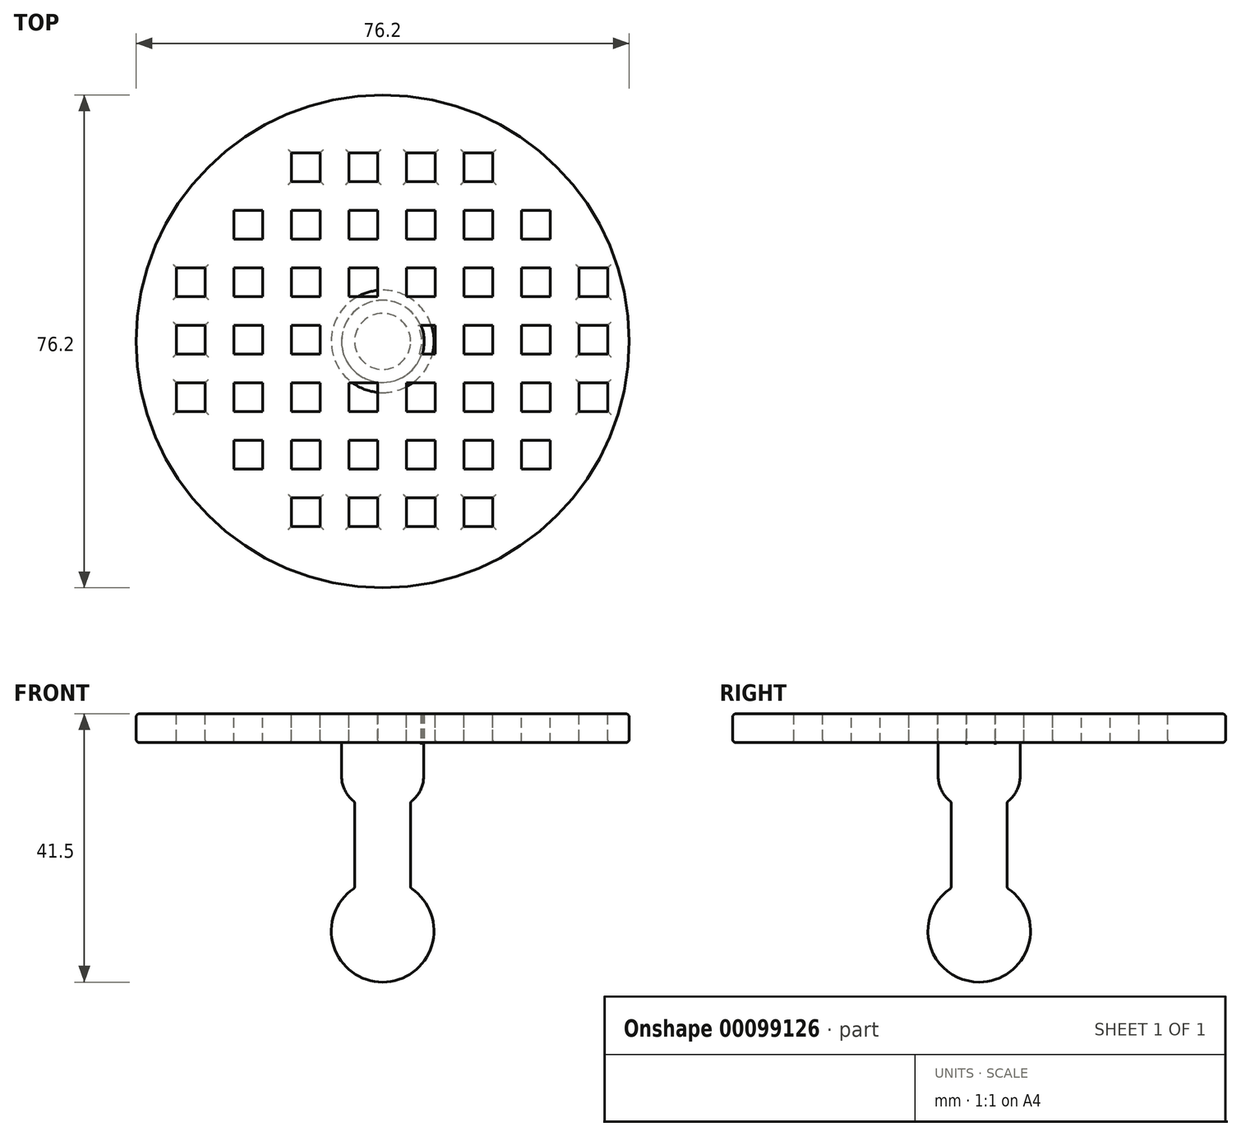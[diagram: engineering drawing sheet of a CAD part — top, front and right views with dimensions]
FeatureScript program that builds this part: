
annotation { "Feature Type Name" : "Feature", "Feature Type Description" : "" }
export const myFeature = defineFeature(function(context is Context, id is Id, definition is map)
    precondition{}
    {
        {
            var Q0;
            Q0=qCreatedBy(makeId("Top.planeOp"),FACE);
            var sketch = newSketch(context, id + "F0", { "sketchPlane" : qUnion([Q0])});
            skCircle(sketch, "E0", {"center": v(0, 0) * mm, "radius": 38.1 * mm});
            skSolve(sketch);
        }
        {
            var Q0;
            Q0=makeQuery(id+"F0.imprint","IMPRINT",FACE,{"disambiguationData":[TD([[makeQuery(id+"F0.imprint","IMPRINT",EDGE,{"derivedFrom":sQuery(id+"F0.wireOp",EDGE,"E0")}),1.0]])]});
            extrude(context, id + "F1", {"entities" : qUnion([Q0]), "depth" : 4.44 * mm});
        }
        {
            var Q0;
            Q0=qCreatedBy(makeId("Top.planeOp"),FACE);
            var sketch = newSketch(context, id + "F2", { "sketchPlane" : qUnion([Q0])});
            skLineSegment(sketch, "E1.bottom", {"start": v(17.03, 29.17) * mm, "end": v(12.58, 29.17) * mm});
            skLineSegment(sketch, "E1.top", {"start": v(17.03, 24.73) * mm, "end": v(12.58, 24.73) * mm});
            skLineSegment(sketch, "E1.left", {"start": v(17.03, 29.17) * mm, "end": v(17.03, 24.73) * mm});
            skLineSegment(sketch, "E1.right", {"start": v(12.58, 29.17) * mm, "end": v(12.58, 24.73) * mm});
            skLineSegment(sketch, "E2.0.1.0", {"start": v(12.58, 20.28) * mm, "end": v(12.58, 15.84) * mm});
            skLineSegment(sketch, "E2.0.1.1", {"start": v(17.03, 20.28) * mm, "end": v(17.03, 15.84) * mm});
            skLineSegment(sketch, "E2.0.1.2", {"start": v(17.03, 20.28) * mm, "end": v(12.58, 20.28) * mm});
            skLineSegment(sketch, "E2.0.1.3", {"start": v(17.03, 15.84) * mm, "end": v(12.58, 15.84) * mm});
            skLineSegment(sketch, "E2.0.2.0", {"start": v(12.58, 11.4) * mm, "end": v(12.58, 6.95) * mm});
            skLineSegment(sketch, "E2.0.2.1", {"start": v(17.03, 11.4) * mm, "end": v(17.03, 6.95) * mm});
            skLineSegment(sketch, "E2.0.2.2", {"start": v(17.03, 11.4) * mm, "end": v(12.58, 11.4) * mm});
            skLineSegment(sketch, "E2.0.2.3", {"start": v(17.03, 6.95) * mm, "end": v(12.58, 6.95) * mm});
            skLineSegment(sketch, "E2.0.3.0", {"start": v(12.58, 2.5) * mm, "end": v(12.58, -1.94) * mm});
            skLineSegment(sketch, "E2.0.3.1", {"start": v(17.03, 2.5) * mm, "end": v(17.03, -1.94) * mm});
            skLineSegment(sketch, "E2.0.3.2", {"start": v(17.03, 2.5) * mm, "end": v(12.58, 2.5) * mm});
            skLineSegment(sketch, "E2.0.3.3", {"start": v(17.03, -1.94) * mm, "end": v(12.58, -1.94) * mm});
            skLineSegment(sketch, "E2.0.4.0", {"start": v(12.58, -6.39) * mm, "end": v(12.58, -10.83) * mm});
            skLineSegment(sketch, "E2.0.4.1", {"start": v(17.03, -6.39) * mm, "end": v(17.03, -10.83) * mm});
            skLineSegment(sketch, "E2.0.4.2", {"start": v(17.03, -6.39) * mm, "end": v(12.58, -6.39) * mm});
            skLineSegment(sketch, "E2.0.4.3", {"start": v(17.03, -10.83) * mm, "end": v(12.58, -10.83) * mm});
            skLineSegment(sketch, "E2.0.5.0", {"start": v(12.58, -15.28) * mm, "end": v(12.58, -19.72) * mm});
            skLineSegment(sketch, "E2.0.5.1", {"start": v(17.03, -15.28) * mm, "end": v(17.03, -19.72) * mm});
            skLineSegment(sketch, "E2.0.5.2", {"start": v(17.03, -15.28) * mm, "end": v(12.58, -15.28) * mm});
            skLineSegment(sketch, "E2.0.5.3", {"start": v(17.03, -19.72) * mm, "end": v(12.58, -19.72) * mm});
            skLineSegment(sketch, "E2.0.6.0", {"start": v(12.58, -24.17) * mm, "end": v(12.58, -28.61) * mm});
            skLineSegment(sketch, "E2.0.6.1", {"start": v(17.03, -24.17) * mm, "end": v(17.03, -28.61) * mm});
            skLineSegment(sketch, "E2.0.6.2", {"start": v(17.03, -24.17) * mm, "end": v(12.58, -24.17) * mm});
            skLineSegment(sketch, "E2.0.6.3", {"start": v(17.03, -28.61) * mm, "end": v(12.58, -28.61) * mm});
            skLineSegment(sketch, "E2.1.0.0", {"start": v(3.7, 29.17) * mm, "end": v(3.7, 24.73) * mm});
            skLineSegment(sketch, "E2.1.0.1", {"start": v(8.14, 29.17) * mm, "end": v(8.14, 24.73) * mm});
            skLineSegment(sketch, "E2.1.0.2", {"start": v(8.14, 29.17) * mm, "end": v(3.7, 29.17) * mm});
            skLineSegment(sketch, "E2.1.0.3", {"start": v(8.14, 24.73) * mm, "end": v(3.7, 24.73) * mm});
            skLineSegment(sketch, "E2.1.1.0", {"start": v(3.7, 20.28) * mm, "end": v(3.7, 15.84) * mm});
            skLineSegment(sketch, "E2.1.1.1", {"start": v(8.14, 20.28) * mm, "end": v(8.14, 15.84) * mm});
            skLineSegment(sketch, "E2.1.1.2", {"start": v(8.14, 20.28) * mm, "end": v(3.7, 20.28) * mm});
            skLineSegment(sketch, "E2.1.1.3", {"start": v(8.14, 15.84) * mm, "end": v(3.7, 15.84) * mm});
            skLineSegment(sketch, "E2.1.2.0", {"start": v(3.7, 11.4) * mm, "end": v(3.7, 6.95) * mm});
            skLineSegment(sketch, "E2.1.2.1", {"start": v(8.14, 11.4) * mm, "end": v(8.14, 6.95) * mm});
            skLineSegment(sketch, "E2.1.2.2", {"start": v(8.14, 11.4) * mm, "end": v(3.7, 11.4) * mm});
            skLineSegment(sketch, "E2.1.2.3", {"start": v(8.14, 6.95) * mm, "end": v(3.7, 6.95) * mm});
            skLineSegment(sketch, "E2.1.3.0", {"start": v(3.7, 2.5) * mm, "end": v(3.7, -1.94) * mm});
            skLineSegment(sketch, "E2.1.3.1", {"start": v(8.14, 2.5) * mm, "end": v(8.14, -1.94) * mm});
            skLineSegment(sketch, "E2.1.3.2", {"start": v(8.14, 2.5) * mm, "end": v(3.7, 2.5) * mm});
            skLineSegment(sketch, "E2.1.3.3", {"start": v(8.14, -1.94) * mm, "end": v(3.7, -1.94) * mm});
            skLineSegment(sketch, "E2.1.4.0", {"start": v(3.7, -6.39) * mm, "end": v(3.7, -10.83) * mm});
            skLineSegment(sketch, "E2.1.4.1", {"start": v(8.14, -6.39) * mm, "end": v(8.14, -10.83) * mm});
            skLineSegment(sketch, "E2.1.4.2", {"start": v(8.14, -6.39) * mm, "end": v(3.7, -6.39) * mm});
            skLineSegment(sketch, "E2.1.4.3", {"start": v(8.14, -10.83) * mm, "end": v(3.7, -10.83) * mm});
            skLineSegment(sketch, "E2.1.5.0", {"start": v(3.7, -15.28) * mm, "end": v(3.7, -19.72) * mm});
            skLineSegment(sketch, "E2.1.5.1", {"start": v(8.14, -15.28) * mm, "end": v(8.14, -19.72) * mm});
            skLineSegment(sketch, "E2.1.5.2", {"start": v(8.14, -15.28) * mm, "end": v(3.7, -15.28) * mm});
            skLineSegment(sketch, "E2.1.5.3", {"start": v(8.14, -19.72) * mm, "end": v(3.7, -19.72) * mm});
            skLineSegment(sketch, "E2.1.6.0", {"start": v(3.7, -24.17) * mm, "end": v(3.7, -28.61) * mm});
            skLineSegment(sketch, "E2.1.6.1", {"start": v(8.14, -24.17) * mm, "end": v(8.14, -28.61) * mm});
            skLineSegment(sketch, "E2.1.6.2", {"start": v(8.14, -24.17) * mm, "end": v(3.7, -24.17) * mm});
            skLineSegment(sketch, "E2.1.6.3", {"start": v(8.14, -28.61) * mm, "end": v(3.7, -28.61) * mm});
            skLineSegment(sketch, "E2.2.0.0", {"start": v(-5.2, 29.17) * mm, "end": v(-5.2, 24.73) * mm});
            skLineSegment(sketch, "E2.2.0.1", {"start": v(-0.75, 29.17) * mm, "end": v(-0.75, 24.73) * mm});
            skLineSegment(sketch, "E2.2.0.2", {"start": v(-0.75, 29.17) * mm, "end": v(-5.2, 29.17) * mm});
            skLineSegment(sketch, "E2.2.0.3", {"start": v(-0.75, 24.73) * mm, "end": v(-5.2, 24.73) * mm});
            skLineSegment(sketch, "E2.2.1.0", {"start": v(-5.2, 20.28) * mm, "end": v(-5.2, 15.84) * mm});
            skLineSegment(sketch, "E2.2.1.1", {"start": v(-0.75, 20.28) * mm, "end": v(-0.75, 15.84) * mm});
            skLineSegment(sketch, "E2.2.1.2", {"start": v(-0.75, 20.28) * mm, "end": v(-5.2, 20.28) * mm});
            skLineSegment(sketch, "E2.2.1.3", {"start": v(-0.75, 15.84) * mm, "end": v(-5.2, 15.84) * mm});
            skLineSegment(sketch, "E2.2.2.0", {"start": v(-5.2, 11.4) * mm, "end": v(-5.2, 6.95) * mm});
            skLineSegment(sketch, "E2.2.2.1", {"start": v(-0.75, 11.4) * mm, "end": v(-0.75, 6.95) * mm});
            skLineSegment(sketch, "E2.2.2.2", {"start": v(-0.75, 11.4) * mm, "end": v(-5.2, 11.4) * mm});
            skLineSegment(sketch, "E2.2.2.3", {"start": v(-0.75, 6.95) * mm, "end": v(-5.2, 6.95) * mm});
            skLineSegment(sketch, "E2.2.3.0", {"start": v(-5.2, 2.5) * mm, "end": v(-5.2, -1.94) * mm});
            skLineSegment(sketch, "E2.2.3.1", {"start": v(-0.75, 2.5) * mm, "end": v(-0.75, -1.94) * mm});
            skLineSegment(sketch, "E2.2.3.2", {"start": v(-0.75, 2.5) * mm, "end": v(-5.2, 2.5) * mm});
            skLineSegment(sketch, "E2.2.3.3", {"start": v(-0.75, -1.94) * mm, "end": v(-5.2, -1.94) * mm});
            skLineSegment(sketch, "E2.2.4.0", {"start": v(-5.2, -6.39) * mm, "end": v(-5.2, -10.83) * mm});
            skLineSegment(sketch, "E2.2.4.1", {"start": v(-0.75, -6.39) * mm, "end": v(-0.75, -10.83) * mm});
            skLineSegment(sketch, "E2.2.4.2", {"start": v(-0.75, -6.39) * mm, "end": v(-5.2, -6.39) * mm});
            skLineSegment(sketch, "E2.2.4.3", {"start": v(-0.75, -10.83) * mm, "end": v(-5.2, -10.83) * mm});
            skLineSegment(sketch, "E2.2.5.0", {"start": v(-5.2, -15.28) * mm, "end": v(-5.2, -19.72) * mm});
            skLineSegment(sketch, "E2.2.5.1", {"start": v(-0.75, -15.28) * mm, "end": v(-0.75, -19.72) * mm});
            skLineSegment(sketch, "E2.2.5.2", {"start": v(-0.75, -15.28) * mm, "end": v(-5.2, -15.28) * mm});
            skLineSegment(sketch, "E2.2.5.3", {"start": v(-0.75, -19.72) * mm, "end": v(-5.2, -19.72) * mm});
            skLineSegment(sketch, "E2.2.6.0", {"start": v(-5.2, -24.17) * mm, "end": v(-5.2, -28.61) * mm});
            skLineSegment(sketch, "E2.2.6.1", {"start": v(-0.75, -24.17) * mm, "end": v(-0.75, -28.61) * mm});
            skLineSegment(sketch, "E2.2.6.2", {"start": v(-0.75, -24.17) * mm, "end": v(-5.2, -24.17) * mm});
            skLineSegment(sketch, "E2.2.6.3", {"start": v(-0.75, -28.61) * mm, "end": v(-5.2, -28.61) * mm});
            skLineSegment(sketch, "E2.3.0.0", {"start": v(-14.09, 29.17) * mm, "end": v(-14.09, 24.73) * mm});
            skLineSegment(sketch, "E2.3.0.1", {"start": v(-9.64, 29.17) * mm, "end": v(-9.64, 24.73) * mm});
            skLineSegment(sketch, "E2.3.0.2", {"start": v(-9.64, 29.17) * mm, "end": v(-14.09, 29.17) * mm});
            skLineSegment(sketch, "E2.3.0.3", {"start": v(-9.64, 24.73) * mm, "end": v(-14.09, 24.73) * mm});
            skLineSegment(sketch, "E2.3.1.0", {"start": v(-14.09, 20.28) * mm, "end": v(-14.09, 15.84) * mm});
            skLineSegment(sketch, "E2.3.1.1", {"start": v(-9.64, 20.28) * mm, "end": v(-9.64, 15.84) * mm});
            skLineSegment(sketch, "E2.3.1.2", {"start": v(-9.64, 20.28) * mm, "end": v(-14.09, 20.28) * mm});
            skLineSegment(sketch, "E2.3.1.3", {"start": v(-9.64, 15.84) * mm, "end": v(-14.09, 15.84) * mm});
            skLineSegment(sketch, "E2.3.2.0", {"start": v(-14.09, 11.4) * mm, "end": v(-14.09, 6.95) * mm});
            skLineSegment(sketch, "E2.3.2.1", {"start": v(-9.64, 11.4) * mm, "end": v(-9.64, 6.95) * mm});
            skLineSegment(sketch, "E2.3.2.2", {"start": v(-9.64, 11.4) * mm, "end": v(-14.09, 11.4) * mm});
            skLineSegment(sketch, "E2.3.2.3", {"start": v(-9.64, 6.95) * mm, "end": v(-14.09, 6.95) * mm});
            skLineSegment(sketch, "E2.3.3.0", {"start": v(-14.09, 2.5) * mm, "end": v(-14.09, -1.94) * mm});
            skLineSegment(sketch, "E2.3.3.1", {"start": v(-9.64, 2.5) * mm, "end": v(-9.64, -1.94) * mm});
            skLineSegment(sketch, "E2.3.3.2", {"start": v(-9.64, 2.5) * mm, "end": v(-14.09, 2.5) * mm});
            skLineSegment(sketch, "E2.3.3.3", {"start": v(-9.64, -1.94) * mm, "end": v(-14.09, -1.94) * mm});
            skLineSegment(sketch, "E2.3.4.0", {"start": v(-14.09, -6.39) * mm, "end": v(-14.09, -10.83) * mm});
            skLineSegment(sketch, "E2.3.4.1", {"start": v(-9.64, -6.39) * mm, "end": v(-9.64, -10.83) * mm});
            skLineSegment(sketch, "E2.3.4.2", {"start": v(-9.64, -6.39) * mm, "end": v(-14.09, -6.39) * mm});
            skLineSegment(sketch, "E2.3.4.3", {"start": v(-9.64, -10.83) * mm, "end": v(-14.09, -10.83) * mm});
            skLineSegment(sketch, "E2.3.5.0", {"start": v(-14.09, -15.28) * mm, "end": v(-14.09, -19.72) * mm});
            skLineSegment(sketch, "E2.3.5.1", {"start": v(-9.64, -15.28) * mm, "end": v(-9.64, -19.72) * mm});
            skLineSegment(sketch, "E2.3.5.2", {"start": v(-9.64, -15.28) * mm, "end": v(-14.09, -15.28) * mm});
            skLineSegment(sketch, "E2.3.5.3", {"start": v(-9.64, -19.72) * mm, "end": v(-14.09, -19.72) * mm});
            skLineSegment(sketch, "E2.3.6.0", {"start": v(-14.09, -24.17) * mm, "end": v(-14.09, -28.61) * mm});
            skLineSegment(sketch, "E2.3.6.1", {"start": v(-9.64, -24.17) * mm, "end": v(-9.64, -28.61) * mm});
            skLineSegment(sketch, "E2.3.6.2", {"start": v(-9.64, -24.17) * mm, "end": v(-14.09, -24.17) * mm});
            skLineSegment(sketch, "E2.3.6.3", {"start": v(-9.64, -28.61) * mm, "end": v(-14.09, -28.61) * mm});
            skLineSegment(sketch, "E2.direction1", {"start": v(12.58, 24.73) * mm, "end": v(3.7, 24.73) * mm, "construction": true});
            skLineSegment(sketch, "E2.direction2", {"start": v(12.58, 24.73) * mm, "end": v(12.58, 15.84) * mm, "construction": true});
            skLineSegment(sketch, "E3.1.0.0", {"start": v(-18.53, 20.28) * mm, "end": v(-22.98, 20.28) * mm});
            skLineSegment(sketch, "E3.1.0.1", {"start": v(-18.53, 15.84) * mm, "end": v(-22.98, 15.84) * mm});
            skLineSegment(sketch, "E3.1.0.2", {"start": v(-18.53, 20.28) * mm, "end": v(-18.53, 15.84) * mm});
            skLineSegment(sketch, "E3.1.0.3", {"start": v(-18.53, 11.4) * mm, "end": v(-22.98, 11.4) * mm});
            skLineSegment(sketch, "E3.1.0.4", {"start": v(-18.53, 11.4) * mm, "end": v(-18.53, 6.95) * mm});
            skLineSegment(sketch, "E3.1.0.5", {"start": v(-22.98, 11.4) * mm, "end": v(-22.98, 6.95) * mm});
            skLineSegment(sketch, "E3.1.0.6", {"start": v(-18.53, 6.95) * mm, "end": v(-22.98, 6.95) * mm});
            skLineSegment(sketch, "E3.1.0.7", {"start": v(-18.53, 2.5) * mm, "end": v(-22.98, 2.5) * mm});
            skLineSegment(sketch, "E3.1.0.8", {"start": v(-18.53, -1.94) * mm, "end": v(-22.98, -1.94) * mm});
            skLineSegment(sketch, "E3.1.0.9", {"start": v(-18.53, 2.5) * mm, "end": v(-18.53, -1.94) * mm});
            skLineSegment(sketch, "E3.1.0.10", {"start": v(-22.98, 2.5) * mm, "end": v(-22.98, -1.94) * mm});
            skLineSegment(sketch, "E3.1.0.11", {"start": v(-18.53, -6.39) * mm, "end": v(-22.98, -6.39) * mm});
            skLineSegment(sketch, "E3.1.0.12", {"start": v(-18.53, -6.39) * mm, "end": v(-18.53, -10.83) * mm});
            skLineSegment(sketch, "E3.1.0.13", {"start": v(-22.98, -6.39) * mm, "end": v(-22.98, -10.83) * mm});
            skLineSegment(sketch, "E3.1.0.14", {"start": v(-18.53, -10.83) * mm, "end": v(-22.98, -10.83) * mm});
            skLineSegment(sketch, "E3.1.0.15", {"start": v(-18.53, -15.28) * mm, "end": v(-22.98, -15.28) * mm});
            skLineSegment(sketch, "E3.1.0.16", {"start": v(-18.53, -15.28) * mm, "end": v(-18.53, -19.72) * mm});
            skLineSegment(sketch, "E3.1.0.17", {"start": v(-22.98, -15.28) * mm, "end": v(-22.98, -19.72) * mm});
            skLineSegment(sketch, "E3.1.0.18", {"start": v(-18.53, -19.72) * mm, "end": v(-22.98, -19.72) * mm});
            skLineSegment(sketch, "E3.direction1", {"start": v(-14.09, 20.28) * mm, "end": v(-22.98, 20.28) * mm, "construction": true});
            skLineSegment(sketch, "E4.1.0.0", {"start": v(25.92, 15.84) * mm, "end": v(21.47, 15.84) * mm});
            skLineSegment(sketch, "E4.1.0.1", {"start": v(25.92, 20.28) * mm, "end": v(21.47, 20.28) * mm});
            skLineSegment(sketch, "E4.1.0.2", {"start": v(25.92, 20.28) * mm, "end": v(25.92, 15.84) * mm});
            skLineSegment(sketch, "E4.1.0.3", {"start": v(21.47, 20.28) * mm, "end": v(21.47, 15.84) * mm});
            skLineSegment(sketch, "E4.1.0.4", {"start": v(21.47, 11.4) * mm, "end": v(21.47, 6.95) * mm});
            skLineSegment(sketch, "E4.1.0.5", {"start": v(25.92, 6.95) * mm, "end": v(21.47, 6.95) * mm});
            skLineSegment(sketch, "E4.1.0.6", {"start": v(25.92, 11.4) * mm, "end": v(21.47, 11.4) * mm});
            skLineSegment(sketch, "E4.1.0.7", {"start": v(25.92, 11.4) * mm, "end": v(25.92, 6.95) * mm});
            skLineSegment(sketch, "E4.1.0.8", {"start": v(25.92, 2.5) * mm, "end": v(21.47, 2.5) * mm});
            skLineSegment(sketch, "E4.1.0.9", {"start": v(21.47, 2.5) * mm, "end": v(21.47, -1.94) * mm});
            skLineSegment(sketch, "E4.1.0.10", {"start": v(25.92, -1.94) * mm, "end": v(21.47, -1.94) * mm});
            skLineSegment(sketch, "E4.1.0.11", {"start": v(25.92, 2.5) * mm, "end": v(25.92, -1.94) * mm});
            skLineSegment(sketch, "E4.1.0.12", {"start": v(25.92, -6.39) * mm, "end": v(21.47, -6.39) * mm});
            skLineSegment(sketch, "E4.1.0.13", {"start": v(25.92, -6.39) * mm, "end": v(25.92, -10.83) * mm});
            skLineSegment(sketch, "E4.1.0.14", {"start": v(21.47, -6.39) * mm, "end": v(21.47, -10.83) * mm});
            skLineSegment(sketch, "E4.1.0.15", {"start": v(25.92, -10.83) * mm, "end": v(21.47, -10.83) * mm});
            skLineSegment(sketch, "E4.1.0.16", {"start": v(25.92, -15.28) * mm, "end": v(21.47, -15.28) * mm});
            skLineSegment(sketch, "E4.1.0.17", {"start": v(21.47, -15.28) * mm, "end": v(21.47, -19.72) * mm});
            skLineSegment(sketch, "E4.1.0.18", {"start": v(25.92, -19.72) * mm, "end": v(21.47, -19.72) * mm});
            skLineSegment(sketch, "E4.1.0.19", {"start": v(25.92, -15.28) * mm, "end": v(25.92, -19.72) * mm});
            skLineSegment(sketch, "E4.direction1", {"start": v(12.58, 15.84) * mm, "end": v(21.47, 15.84) * mm, "construction": true});
            skLineSegment(sketch, "E5.1.0.0", {"start": v(-31.87, 11.4) * mm, "end": v(-31.87, 6.95) * mm});
            skLineSegment(sketch, "E5.1.0.1", {"start": v(-27.42, 11.4) * mm, "end": v(-31.87, 11.4) * mm});
            skLineSegment(sketch, "E5.1.0.2", {"start": v(-27.42, 11.4) * mm, "end": v(-27.42, 6.95) * mm});
            skLineSegment(sketch, "E5.1.0.3", {"start": v(-27.42, 6.95) * mm, "end": v(-31.87, 6.95) * mm});
            skLineSegment(sketch, "E5.1.0.4", {"start": v(-27.42, 2.5) * mm, "end": v(-31.87, 2.5) * mm});
            skLineSegment(sketch, "E5.1.0.5", {"start": v(-31.87, 2.5) * mm, "end": v(-31.87, -1.94) * mm});
            skLineSegment(sketch, "E5.1.0.6", {"start": v(-27.42, -1.94) * mm, "end": v(-31.87, -1.94) * mm});
            skLineSegment(sketch, "E5.1.0.7", {"start": v(-27.42, 2.5) * mm, "end": v(-27.42, -1.94) * mm});
            skLineSegment(sketch, "E5.1.0.8", {"start": v(-27.42, -6.39) * mm, "end": v(-31.87, -6.39) * mm});
            skLineSegment(sketch, "E5.1.0.9", {"start": v(-27.42, -10.83) * mm, "end": v(-31.87, -10.83) * mm});
            skLineSegment(sketch, "E5.1.0.10", {"start": v(-31.87, -6.39) * mm, "end": v(-31.87, -10.83) * mm});
            skLineSegment(sketch, "E5.1.0.11", {"start": v(-27.42, -6.39) * mm, "end": v(-27.42, -10.83) * mm});
            skLineSegment(sketch, "E5.direction1", {"start": v(-22.98, 6.95) * mm, "end": v(-31.87, 6.95) * mm, "construction": true});
            skLineSegment(sketch, "E6.1.0.0", {"start": v(34.8, 11.4) * mm, "end": v(30.36, 11.4) * mm});
            skLineSegment(sketch, "E6.1.0.1", {"start": v(34.8, 6.95) * mm, "end": v(30.36, 6.95) * mm});
            skLineSegment(sketch, "E6.1.0.2", {"start": v(30.36, 11.4) * mm, "end": v(30.36, 6.95) * mm});
            skLineSegment(sketch, "E6.1.0.3", {"start": v(34.8, 11.4) * mm, "end": v(34.8, 6.95) * mm});
            skLineSegment(sketch, "E6.1.0.4", {"start": v(34.8, 2.5) * mm, "end": v(30.36, 2.5) * mm});
            skLineSegment(sketch, "E6.1.0.5", {"start": v(34.8, 2.5) * mm, "end": v(34.8, -1.94) * mm});
            skLineSegment(sketch, "E6.1.0.6", {"start": v(30.36, 2.5) * mm, "end": v(30.36, -1.94) * mm});
            skLineSegment(sketch, "E6.1.0.7", {"start": v(34.8, -1.94) * mm, "end": v(30.36, -1.94) * mm});
            skLineSegment(sketch, "E6.1.0.8", {"start": v(34.8, -6.39) * mm, "end": v(30.36, -6.39) * mm});
            skLineSegment(sketch, "E6.1.0.9", {"start": v(30.36, -6.39) * mm, "end": v(30.36, -10.83) * mm});
            skLineSegment(sketch, "E6.1.0.10", {"start": v(34.8, -6.39) * mm, "end": v(34.8, -10.83) * mm});
            skLineSegment(sketch, "E6.direction1", {"start": v(21.47, 11.4) * mm, "end": v(30.36, 11.4) * mm, "construction": true});
            skLineSegment(sketch, "E7", {"start": v(34.8, -10.83) * mm, "end": v(30.36, -10.83) * mm});
            skLineSegment(sketch, "E8", {"start": v(-22.98, 20.28) * mm, "end": v(-22.98, 15.84) * mm});
            skSolve(sketch);
        }
        {
            var Q0;
            Q0 = qSketchRegion(id + "F2", true);
            extrude(context, id + "F3", {"entities" : qUnion([Q0]), "operationType" : NewBodyOperationType.REMOVE, "endBound" : BoundingType.SYMMETRIC, "oppositeDirection" : true, "depth" : 25.4 * mm});
        }
        {
            var Q0;
            Q0=qCreatedBy(makeId("Right.planeOp"),FACE);
            var sketch = newSketch(context, id + "F4", { "sketchPlane" : qUnion([Q0])});
            skLineSegment(sketch, "E9", {"start": v(0, 0) * mm, "end": v(-6.35, 0) * mm});
            skLineSegment(sketch, "E10", {"start": v(-6.35, 0) * mm, "end": v(-6.35, -9.2) * mm});
            skLineSegment(sketch, "E11", {"start": v(-6.35, -9.2) * mm, "end": v(-4.34, -9.2) * mm});
            skLineSegment(sketch, "E12", {"start": v(-4.34, -9.2) * mm, "end": v(-4.34, -22.53) * mm});
            skArc(sketch, "E13", {"start": v(-7.93, -29.12) * mm, "mid": v(-6.97, -25.34) * mm, "end": v(-4.34, -22.48) * mm});
            skPoint(sketch, "E13.startSnap0", {"position": v(-2.3, -29.12) * mm});
            skArc(sketch, "E14", {"start": v(-7.93, -29.12) * mm, "mid": v(-5.6, -34.72) * mm, "end": v(0, -37.05) * mm});
            skLineSegment(sketch, "E15", {"start": v(0, -37.05) * mm, "end": v(0, 0) * mm});
            skSolve(sketch);
        }
        {
            var Q0;
            Q0 = qSketchRegion(id + "F4", true);
            var Q1;
            Q1=sQuery(id+"F4.wireOp",EDGE,"E15");
            revolve(context, id + "F5", {"operationType" : NewBodyOperationType.ADD, "entities" : qUnion([Q0]), "axis" : qUnion([Q1]), "revolveType" : RevolveType.FULL});
        }
        {
            var Q0;
            Q0=makeQuery(id+"F5.opRevolve","SWEPT_EDGE",EDGE,{"disambiguationData":[OSD([sQuery(id+"F4.wireOp",EDGE,"E10"),sQuery(id+"F4.wireOp",EDGE,"E11")])]});
            fillet(context, id + "F6", {"entities" : qUnion([Q0]), "radius" : 5.08 * mm, "tangentPropagation" : true, "allowEdgeOverflow" : false});
        }
        {
            var Q0;
            Q0=makeQuery(id+"F6.opFillet","BLEND_EDGE",EDGE,{"blendedFrom":[makeQuery(id+"F5.opRevolve","SWEPT_EDGE",EDGE,{"disambiguationData":[OSD([sQuery(id+"F4.wireOp",EDGE,"E10"),sQuery(id+"F4.wireOp",EDGE,"E11")])]}),makeQuery(id+"F5.opRevolve","SWEPT_FACE",FACE,{"disambiguationData":[OSD([sQuery(id+"F4.wireOp",EDGE,"E12")])]})],"blendedInto":[makeQuery(id+"F5.opRevolve","SWEPT_FACE",FACE,{"disambiguationData":[OSD([sQuery(id+"F4.wireOp",EDGE,"E12")])]})]});
            var Q1;
            Q1=makeQuery(id+"F5.opRevolve","SWEPT_EDGE",EDGE,{"disambiguationData":[OSD([sQuery(id+"F4.wireOp",EDGE,"E12"),sQuery(id+"F4.wireOp",EDGE,"E13")])]});
            var Q2;
            {var subQ0=sQuery(id+"F4.wireOp",EDGE,"E10");Q2=makeQuery(id+"F5.boolean.opBoolean","SPLIT",EDGE,{"disambiguationData":[topologyDisambiguationEdgeConnected([makeQuery(id+"F1.opExtrude","CAP_FACE",FACE,{"disambiguationData":[OSD([sQuery(id+"F0.wireOp",EDGE,"E0")])],"isStart":true})])],"derivedFrom":makeQuery(id+"F5.opRevolve","SWEPT_EDGE",EDGE,{"disambiguationData":[OSD([sQuery(id+"F4.wireOp",EDGE,"E9"),subQ0])]})});}
            fillet(context, id + "F7", {"entities" : qUnion([Q0, Q1, Q2]), "radius" : 0.32 * mm, "tangentPropagation" : true, "allowEdgeOverflow" : false});
        }
        {
            var Q0;
            Q0=makeQuery(id+"F5.boolean.opBoolean","SPLIT",FACE,{"disambiguationData":[TD([makeQuery(id+"F1.opExtrude","CAP_FACE",FACE,{"disambiguationData":[OSD([sQuery(id+"F0.wireOp",EDGE,"E0")])],"isStart":true})])],"derivedFrom":makeQuery(id+"F5.opRevolve","SWEPT_FACE",FACE,{"disambiguationData":[OSD([sQuery(id+"F4.wireOp",EDGE,"E9")])]})});
            var sketch = newSketch(context, id + "F8", { "sketchPlane" : qUnion([Q0])});
            skCircle(sketch, "E16", {"center": v(0, 0) * mm, "radius": 6.43 * mm});
            skSolve(sketch);
        }
        {
            var Q0;
            Q0 = qSketchRegion(id + "F8", true);
            extrude(context, id + "F9", {"entities" : qUnion([Q0]), "operationType" : NewBodyOperationType.ADD, "depth" : 4.44 * mm});
        }
        {
            var Q0;
            Q0=makeQuery(id+"F1.opExtrude","CAP_EDGE",EDGE,{"disambiguationData":[OSD([sQuery(id+"F0.wireOp",EDGE,"E0")])],"isStart":true});
            var Q1;
            Q1=makeQuery(id+"F1.opExtrude","CAP_EDGE",EDGE,{"disambiguationData":[OSD([sQuery(id+"F0.wireOp",EDGE,"E0")])],"isStart":false});
            fillet(context, id + "F10", {"entities" : qUnion([Q0, Q1]), "radius" : 0.5 * mm, "tangentPropagation" : true, "allowEdgeOverflow" : false});
        }
        {
            var Q0;
            Q0=makeQuery(id+"F3.boolean.opBoolean","INTERSECT",EDGE,{"derivedFrom":[makeQuery(id+"F1.opExtrude","CAP_FACE",FACE,{"disambiguationData":[OSD([sQuery(id+"F0.wireOp",EDGE,"E0")])],"isStart":true}),makeQuery(id+"F3.opExtrude","SWEPT_FACE",FACE,{"disambiguationData":[OSD([sQuery(id+"F2.wireOp",EDGE,"E2.3.6.2")])]})]});
            var Q1;
            Q1=makeQuery(id+"F3.boolean.opBoolean","INTERSECT",EDGE,{"derivedFrom":[makeQuery(id+"F1.opExtrude","CAP_FACE",FACE,{"disambiguationData":[OSD([sQuery(id+"F0.wireOp",EDGE,"E0")])],"isStart":true}),makeQuery(id+"F3.opExtrude","SWEPT_FACE",FACE,{"disambiguationData":[OSD([sQuery(id+"F2.wireOp",EDGE,"E2.3.6.1")])]})]});
            var Q2;
            Q2=makeQuery(id+"F3.boolean.opBoolean","INTERSECT",EDGE,{"derivedFrom":[makeQuery(id+"F1.opExtrude","CAP_FACE",FACE,{"disambiguationData":[OSD([sQuery(id+"F0.wireOp",EDGE,"E0")])],"isStart":true}),makeQuery(id+"F3.opExtrude","SWEPT_FACE",FACE,{"disambiguationData":[OSD([sQuery(id+"F2.wireOp",EDGE,"E2.3.6.3")])]})]});
            var Q3;
            Q3=makeQuery(id+"F3.boolean.opBoolean","INTERSECT",EDGE,{"derivedFrom":[makeQuery(id+"F1.opExtrude","CAP_FACE",FACE,{"disambiguationData":[OSD([sQuery(id+"F0.wireOp",EDGE,"E0")])],"isStart":true}),makeQuery(id+"F3.opExtrude","SWEPT_FACE",FACE,{"disambiguationData":[OSD([sQuery(id+"F2.wireOp",EDGE,"E2.3.6.0")])]})]});
            var Q4;
            Q4=makeQuery(id+"F3.boolean.opBoolean","INTERSECT",EDGE,{"derivedFrom":[makeQuery(id+"F1.opExtrude","CAP_FACE",FACE,{"disambiguationData":[OSD([sQuery(id+"F0.wireOp",EDGE,"E0")])],"isStart":true}),makeQuery(id+"F3.opExtrude","SWEPT_FACE",FACE,{"disambiguationData":[OSD([sQuery(id+"F2.wireOp",EDGE,"E2.2.6.0")])]})]});
            var Q5;
            Q5=makeQuery(id+"F3.boolean.opBoolean","INTERSECT",EDGE,{"derivedFrom":[makeQuery(id+"F1.opExtrude","CAP_FACE",FACE,{"disambiguationData":[OSD([sQuery(id+"F0.wireOp",EDGE,"E0")])],"isStart":true}),makeQuery(id+"F3.opExtrude","SWEPT_FACE",FACE,{"disambiguationData":[OSD([sQuery(id+"F2.wireOp",EDGE,"E2.2.6.3")])]})]});
            var Q6;
            Q6=makeQuery(id+"F3.boolean.opBoolean","INTERSECT",EDGE,{"derivedFrom":[makeQuery(id+"F1.opExtrude","CAP_FACE",FACE,{"disambiguationData":[OSD([sQuery(id+"F0.wireOp",EDGE,"E0")])],"isStart":true}),makeQuery(id+"F3.opExtrude","SWEPT_FACE",FACE,{"disambiguationData":[OSD([sQuery(id+"F2.wireOp",EDGE,"E2.2.6.1")])]})]});
            var Q7;
            Q7=makeQuery(id+"F3.boolean.opBoolean","INTERSECT",EDGE,{"derivedFrom":[makeQuery(id+"F1.opExtrude","CAP_FACE",FACE,{"disambiguationData":[OSD([sQuery(id+"F0.wireOp",EDGE,"E0")])],"isStart":true}),makeQuery(id+"F3.opExtrude","SWEPT_FACE",FACE,{"disambiguationData":[OSD([sQuery(id+"F2.wireOp",EDGE,"E2.2.6.2")])]})]});
            var Q8;
            Q8=makeQuery(id+"F3.boolean.opBoolean","INTERSECT",EDGE,{"derivedFrom":[makeQuery(id+"F1.opExtrude","CAP_FACE",FACE,{"disambiguationData":[OSD([sQuery(id+"F0.wireOp",EDGE,"E0")])],"isStart":true}),makeQuery(id+"F3.opExtrude","SWEPT_FACE",FACE,{"disambiguationData":[OSD([sQuery(id+"F2.wireOp",EDGE,"E2.1.6.0")])]})]});
            var Q9;
            Q9=makeQuery(id+"F3.boolean.opBoolean","INTERSECT",EDGE,{"derivedFrom":[makeQuery(id+"F1.opExtrude","CAP_FACE",FACE,{"disambiguationData":[OSD([sQuery(id+"F0.wireOp",EDGE,"E0")])],"isStart":true}),makeQuery(id+"F3.opExtrude","SWEPT_FACE",FACE,{"disambiguationData":[OSD([sQuery(id+"F2.wireOp",EDGE,"E2.1.6.3")])]})]});
            var Q10;
            Q10=makeQuery(id+"F3.boolean.opBoolean","INTERSECT",EDGE,{"derivedFrom":[makeQuery(id+"F1.opExtrude","CAP_FACE",FACE,{"disambiguationData":[OSD([sQuery(id+"F0.wireOp",EDGE,"E0")])],"isStart":true}),makeQuery(id+"F3.opExtrude","SWEPT_FACE",FACE,{"disambiguationData":[OSD([sQuery(id+"F2.wireOp",EDGE,"E2.1.6.1")])]})]});
            var Q11;
            Q11=makeQuery(id+"F3.boolean.opBoolean","INTERSECT",EDGE,{"derivedFrom":[makeQuery(id+"F1.opExtrude","CAP_FACE",FACE,{"disambiguationData":[OSD([sQuery(id+"F0.wireOp",EDGE,"E0")])],"isStart":true}),makeQuery(id+"F3.opExtrude","SWEPT_FACE",FACE,{"disambiguationData":[OSD([sQuery(id+"F2.wireOp",EDGE,"E2.1.6.2")])]})]});
            var Q12;
            Q12=makeQuery(id+"F3.boolean.opBoolean","INTERSECT",EDGE,{"derivedFrom":[makeQuery(id+"F1.opExtrude","CAP_FACE",FACE,{"disambiguationData":[OSD([sQuery(id+"F0.wireOp",EDGE,"E0")])],"isStart":true}),makeQuery(id+"F3.opExtrude","SWEPT_FACE",FACE,{"disambiguationData":[OSD([sQuery(id+"F2.wireOp",EDGE,"E2.0.6.0")])]})]});
            var Q13;
            Q13=makeQuery(id+"F3.boolean.opBoolean","INTERSECT",EDGE,{"derivedFrom":[makeQuery(id+"F1.opExtrude","CAP_FACE",FACE,{"disambiguationData":[OSD([sQuery(id+"F0.wireOp",EDGE,"E0")])],"isStart":true}),makeQuery(id+"F3.opExtrude","SWEPT_FACE",FACE,{"disambiguationData":[OSD([sQuery(id+"F2.wireOp",EDGE,"E2.0.6.3")])]})]});
            var Q14;
            Q14=makeQuery(id+"F3.boolean.opBoolean","INTERSECT",EDGE,{"derivedFrom":[makeQuery(id+"F1.opExtrude","CAP_FACE",FACE,{"disambiguationData":[OSD([sQuery(id+"F0.wireOp",EDGE,"E0")])],"isStart":true}),makeQuery(id+"F3.opExtrude","SWEPT_FACE",FACE,{"disambiguationData":[OSD([sQuery(id+"F2.wireOp",EDGE,"E2.0.6.1")])]})]});
            var Q15;
            Q15=makeQuery(id+"F3.boolean.opBoolean","INTERSECT",EDGE,{"derivedFrom":[makeQuery(id+"F1.opExtrude","CAP_FACE",FACE,{"disambiguationData":[OSD([sQuery(id+"F0.wireOp",EDGE,"E0")])],"isStart":true}),makeQuery(id+"F3.opExtrude","SWEPT_FACE",FACE,{"disambiguationData":[OSD([sQuery(id+"F2.wireOp",EDGE,"E2.0.6.2")])]})]});
            var Q16;
            Q16=makeQuery(id+"F3.boolean.opBoolean","INTERSECT",EDGE,{"derivedFrom":[makeQuery(id+"F1.opExtrude","CAP_FACE",FACE,{"disambiguationData":[OSD([sQuery(id+"F0.wireOp",EDGE,"E0")])],"isStart":true}),makeQuery(id+"F3.opExtrude","SWEPT_FACE",FACE,{"disambiguationData":[OSD([sQuery(id+"F2.wireOp",EDGE,"E5.1.0.8")])]})]});
            var Q17;
            Q17=makeQuery(id+"F3.boolean.opBoolean","INTERSECT",EDGE,{"derivedFrom":[makeQuery(id+"F1.opExtrude","CAP_FACE",FACE,{"disambiguationData":[OSD([sQuery(id+"F0.wireOp",EDGE,"E0")])],"isStart":true}),makeQuery(id+"F3.opExtrude","SWEPT_FACE",FACE,{"disambiguationData":[OSD([sQuery(id+"F2.wireOp",EDGE,"E5.1.0.11")])]})]});
            var Q18;
            Q18=makeQuery(id+"F3.boolean.opBoolean","INTERSECT",EDGE,{"derivedFrom":[makeQuery(id+"F1.opExtrude","CAP_FACE",FACE,{"disambiguationData":[OSD([sQuery(id+"F0.wireOp",EDGE,"E0")])],"isStart":true}),makeQuery(id+"F3.opExtrude","SWEPT_FACE",FACE,{"disambiguationData":[OSD([sQuery(id+"F2.wireOp",EDGE,"E5.1.0.9")])]})]});
            var Q19;
            Q19=makeQuery(id+"F3.boolean.opBoolean","INTERSECT",EDGE,{"derivedFrom":[makeQuery(id+"F1.opExtrude","CAP_FACE",FACE,{"disambiguationData":[OSD([sQuery(id+"F0.wireOp",EDGE,"E0")])],"isStart":true}),makeQuery(id+"F3.opExtrude","SWEPT_FACE",FACE,{"disambiguationData":[OSD([sQuery(id+"F2.wireOp",EDGE,"E5.1.0.10")])]})]});
            var Q20;
            Q20=makeQuery(id+"F3.boolean.opBoolean","INTERSECT",EDGE,{"derivedFrom":[makeQuery(id+"F1.opExtrude","CAP_FACE",FACE,{"disambiguationData":[OSD([sQuery(id+"F0.wireOp",EDGE,"E0")])],"isStart":true}),makeQuery(id+"F3.opExtrude","SWEPT_FACE",FACE,{"disambiguationData":[OSD([sQuery(id+"F2.wireOp",EDGE,"E5.1.0.6")])]})]});
            var Q21;
            Q21=makeQuery(id+"F3.boolean.opBoolean","INTERSECT",EDGE,{"derivedFrom":[makeQuery(id+"F1.opExtrude","CAP_FACE",FACE,{"disambiguationData":[OSD([sQuery(id+"F0.wireOp",EDGE,"E0")])],"isStart":true}),makeQuery(id+"F3.opExtrude","SWEPT_FACE",FACE,{"disambiguationData":[OSD([sQuery(id+"F2.wireOp",EDGE,"E5.1.0.7")])]})]});
            var Q22;
            Q22=makeQuery(id+"F3.boolean.opBoolean","INTERSECT",EDGE,{"derivedFrom":[makeQuery(id+"F1.opExtrude","CAP_FACE",FACE,{"disambiguationData":[OSD([sQuery(id+"F0.wireOp",EDGE,"E0")])],"isStart":true}),makeQuery(id+"F3.opExtrude","SWEPT_FACE",FACE,{"disambiguationData":[OSD([sQuery(id+"F2.wireOp",EDGE,"E5.1.0.4")])]})]});
            var Q23;
            Q23=makeQuery(id+"F3.boolean.opBoolean","INTERSECT",EDGE,{"derivedFrom":[makeQuery(id+"F1.opExtrude","CAP_FACE",FACE,{"disambiguationData":[OSD([sQuery(id+"F0.wireOp",EDGE,"E0")])],"isStart":true}),makeQuery(id+"F3.opExtrude","SWEPT_FACE",FACE,{"disambiguationData":[OSD([sQuery(id+"F2.wireOp",EDGE,"E5.1.0.5")])]})]});
            var Q24;
            Q24=makeQuery(id+"F3.boolean.opBoolean","INTERSECT",EDGE,{"derivedFrom":[makeQuery(id+"F1.opExtrude","CAP_FACE",FACE,{"disambiguationData":[OSD([sQuery(id+"F0.wireOp",EDGE,"E0")])],"isStart":true}),makeQuery(id+"F3.opExtrude","SWEPT_FACE",FACE,{"disambiguationData":[OSD([sQuery(id+"F2.wireOp",EDGE,"E5.1.0.3")])]})]});
            var Q25;
            Q25=makeQuery(id+"F3.boolean.opBoolean","INTERSECT",EDGE,{"derivedFrom":[makeQuery(id+"F1.opExtrude","CAP_FACE",FACE,{"disambiguationData":[OSD([sQuery(id+"F0.wireOp",EDGE,"E0")])],"isStart":true}),makeQuery(id+"F3.opExtrude","SWEPT_FACE",FACE,{"disambiguationData":[OSD([sQuery(id+"F2.wireOp",EDGE,"E5.1.0.2")])]})]});
            var Q26;
            Q26=makeQuery(id+"F3.boolean.opBoolean","INTERSECT",EDGE,{"derivedFrom":[makeQuery(id+"F1.opExtrude","CAP_FACE",FACE,{"disambiguationData":[OSD([sQuery(id+"F0.wireOp",EDGE,"E0")])],"isStart":true}),makeQuery(id+"F3.opExtrude","SWEPT_FACE",FACE,{"disambiguationData":[OSD([sQuery(id+"F2.wireOp",EDGE,"E5.1.0.1")])]})]});
            var Q27;
            Q27=makeQuery(id+"F3.boolean.opBoolean","INTERSECT",EDGE,{"derivedFrom":[makeQuery(id+"F1.opExtrude","CAP_FACE",FACE,{"disambiguationData":[OSD([sQuery(id+"F0.wireOp",EDGE,"E0")])],"isStart":true}),makeQuery(id+"F3.opExtrude","SWEPT_FACE",FACE,{"disambiguationData":[OSD([sQuery(id+"F2.wireOp",EDGE,"E5.1.0.0")])]})]});
            var Q28;
            Q28=makeQuery(id+"F3.boolean.opBoolean","INTERSECT",EDGE,{"derivedFrom":[makeQuery(id+"F1.opExtrude","CAP_FACE",FACE,{"disambiguationData":[OSD([sQuery(id+"F0.wireOp",EDGE,"E0")])],"isStart":true}),makeQuery(id+"F3.opExtrude","SWEPT_FACE",FACE,{"disambiguationData":[OSD([sQuery(id+"F2.wireOp",EDGE,"E2.3.0.2")])]})]});
            var Q29;
            Q29=makeQuery(id+"F3.boolean.opBoolean","INTERSECT",EDGE,{"derivedFrom":[makeQuery(id+"F1.opExtrude","CAP_FACE",FACE,{"disambiguationData":[OSD([sQuery(id+"F0.wireOp",EDGE,"E0")])],"isStart":true}),makeQuery(id+"F3.opExtrude","SWEPT_FACE",FACE,{"disambiguationData":[OSD([sQuery(id+"F2.wireOp",EDGE,"E2.3.0.0")])]})]});
            var Q30;
            Q30=makeQuery(id+"F3.boolean.opBoolean","INTERSECT",EDGE,{"derivedFrom":[makeQuery(id+"F1.opExtrude","CAP_FACE",FACE,{"disambiguationData":[OSD([sQuery(id+"F0.wireOp",EDGE,"E0")])],"isStart":true}),makeQuery(id+"F3.opExtrude","SWEPT_FACE",FACE,{"disambiguationData":[OSD([sQuery(id+"F2.wireOp",EDGE,"E2.3.0.3")])]})]});
            var Q31;
            Q31=makeQuery(id+"F3.boolean.opBoolean","INTERSECT",EDGE,{"derivedFrom":[makeQuery(id+"F1.opExtrude","CAP_FACE",FACE,{"disambiguationData":[OSD([sQuery(id+"F0.wireOp",EDGE,"E0")])],"isStart":true}),makeQuery(id+"F3.opExtrude","SWEPT_FACE",FACE,{"disambiguationData":[OSD([sQuery(id+"F2.wireOp",EDGE,"E2.3.0.1")])]})]});
            var Q32;
            Q32=makeQuery(id+"F3.boolean.opBoolean","INTERSECT",EDGE,{"derivedFrom":[makeQuery(id+"F1.opExtrude","CAP_FACE",FACE,{"disambiguationData":[OSD([sQuery(id+"F0.wireOp",EDGE,"E0")])],"isStart":true}),makeQuery(id+"F3.opExtrude","SWEPT_FACE",FACE,{"disambiguationData":[OSD([sQuery(id+"F2.wireOp",EDGE,"E2.2.0.2")])]})]});
            var Q33;
            Q33=makeQuery(id+"F3.boolean.opBoolean","INTERSECT",EDGE,{"derivedFrom":[makeQuery(id+"F1.opExtrude","CAP_FACE",FACE,{"disambiguationData":[OSD([sQuery(id+"F0.wireOp",EDGE,"E0")])],"isStart":true}),makeQuery(id+"F3.opExtrude","SWEPT_FACE",FACE,{"disambiguationData":[OSD([sQuery(id+"F2.wireOp",EDGE,"E2.2.0.0")])]})]});
            var Q34;
            Q34=makeQuery(id+"F3.boolean.opBoolean","INTERSECT",EDGE,{"derivedFrom":[makeQuery(id+"F1.opExtrude","CAP_FACE",FACE,{"disambiguationData":[OSD([sQuery(id+"F0.wireOp",EDGE,"E0")])],"isStart":true}),makeQuery(id+"F3.opExtrude","SWEPT_FACE",FACE,{"disambiguationData":[OSD([sQuery(id+"F2.wireOp",EDGE,"E2.2.0.3")])]})]});
            var Q35;
            Q35=makeQuery(id+"F3.boolean.opBoolean","INTERSECT",EDGE,{"derivedFrom":[makeQuery(id+"F1.opExtrude","CAP_FACE",FACE,{"disambiguationData":[OSD([sQuery(id+"F0.wireOp",EDGE,"E0")])],"isStart":true}),makeQuery(id+"F3.opExtrude","SWEPT_FACE",FACE,{"disambiguationData":[OSD([sQuery(id+"F2.wireOp",EDGE,"E2.2.0.1")])]})]});
            var Q36;
            Q36=makeQuery(id+"F3.boolean.opBoolean","INTERSECT",EDGE,{"derivedFrom":[makeQuery(id+"F1.opExtrude","CAP_FACE",FACE,{"disambiguationData":[OSD([sQuery(id+"F0.wireOp",EDGE,"E0")])],"isStart":true}),makeQuery(id+"F3.opExtrude","SWEPT_FACE",FACE,{"disambiguationData":[OSD([sQuery(id+"F2.wireOp",EDGE,"E2.1.0.2")])]})]});
            var Q37;
            Q37=makeQuery(id+"F3.boolean.opBoolean","INTERSECT",EDGE,{"derivedFrom":[makeQuery(id+"F1.opExtrude","CAP_FACE",FACE,{"disambiguationData":[OSD([sQuery(id+"F0.wireOp",EDGE,"E0")])],"isStart":true}),makeQuery(id+"F3.opExtrude","SWEPT_FACE",FACE,{"disambiguationData":[OSD([sQuery(id+"F2.wireOp",EDGE,"E2.1.0.0")])]})]});
            var Q38;
            Q38=makeQuery(id+"F3.boolean.opBoolean","INTERSECT",EDGE,{"derivedFrom":[makeQuery(id+"F1.opExtrude","CAP_FACE",FACE,{"disambiguationData":[OSD([sQuery(id+"F0.wireOp",EDGE,"E0")])],"isStart":true}),makeQuery(id+"F3.opExtrude","SWEPT_FACE",FACE,{"disambiguationData":[OSD([sQuery(id+"F2.wireOp",EDGE,"E2.1.0.3")])]})]});
            var Q39;
            Q39=makeQuery(id+"F3.boolean.opBoolean","INTERSECT",EDGE,{"derivedFrom":[makeQuery(id+"F1.opExtrude","CAP_FACE",FACE,{"disambiguationData":[OSD([sQuery(id+"F0.wireOp",EDGE,"E0")])],"isStart":true}),makeQuery(id+"F3.opExtrude","SWEPT_FACE",FACE,{"disambiguationData":[OSD([sQuery(id+"F2.wireOp",EDGE,"E2.1.0.1")])]})]});
            var Q40;
            Q40=makeQuery(id+"F3.boolean.opBoolean","INTERSECT",EDGE,{"derivedFrom":[makeQuery(id+"F1.opExtrude","CAP_FACE",FACE,{"disambiguationData":[OSD([sQuery(id+"F0.wireOp",EDGE,"E0")])],"isStart":true}),makeQuery(id+"F3.opExtrude","SWEPT_FACE",FACE,{"disambiguationData":[OSD([sQuery(id+"F2.wireOp",EDGE,"E1.bottom")])]})]});
            var Q41;
            Q41=makeQuery(id+"F3.boolean.opBoolean","INTERSECT",EDGE,{"derivedFrom":[makeQuery(id+"F1.opExtrude","CAP_FACE",FACE,{"disambiguationData":[OSD([sQuery(id+"F0.wireOp",EDGE,"E0")])],"isStart":true}),makeQuery(id+"F3.opExtrude","SWEPT_FACE",FACE,{"disambiguationData":[OSD([sQuery(id+"F2.wireOp",EDGE,"E1.right")])]})]});
            var Q42;
            Q42=makeQuery(id+"F3.boolean.opBoolean","INTERSECT",EDGE,{"derivedFrom":[makeQuery(id+"F1.opExtrude","CAP_FACE",FACE,{"disambiguationData":[OSD([sQuery(id+"F0.wireOp",EDGE,"E0")])],"isStart":true}),makeQuery(id+"F3.opExtrude","SWEPT_FACE",FACE,{"disambiguationData":[OSD([sQuery(id+"F2.wireOp",EDGE,"E1.top")])]})]});
            var Q43;
            Q43=makeQuery(id+"F3.boolean.opBoolean","INTERSECT",EDGE,{"derivedFrom":[makeQuery(id+"F1.opExtrude","CAP_FACE",FACE,{"disambiguationData":[OSD([sQuery(id+"F0.wireOp",EDGE,"E0")])],"isStart":true}),makeQuery(id+"F3.opExtrude","SWEPT_FACE",FACE,{"disambiguationData":[OSD([sQuery(id+"F2.wireOp",EDGE,"E1.left")])]})]});
            var Q44;
            Q44=makeQuery(id+"F3.boolean.opBoolean","INTERSECT",EDGE,{"derivedFrom":[makeQuery(id+"F1.opExtrude","CAP_FACE",FACE,{"disambiguationData":[OSD([sQuery(id+"F0.wireOp",EDGE,"E0")])],"isStart":true}),makeQuery(id+"F3.opExtrude","SWEPT_FACE",FACE,{"disambiguationData":[OSD([sQuery(id+"F2.wireOp",EDGE,"E6.1.0.0")])]})]});
            var Q45;
            Q45=makeQuery(id+"F3.boolean.opBoolean","INTERSECT",EDGE,{"derivedFrom":[makeQuery(id+"F1.opExtrude","CAP_FACE",FACE,{"disambiguationData":[OSD([sQuery(id+"F0.wireOp",EDGE,"E0")])],"isStart":true}),makeQuery(id+"F3.opExtrude","SWEPT_FACE",FACE,{"disambiguationData":[OSD([sQuery(id+"F2.wireOp",EDGE,"E6.1.0.3")])]})]});
            var Q46;
            Q46=makeQuery(id+"F3.boolean.opBoolean","INTERSECT",EDGE,{"derivedFrom":[makeQuery(id+"F1.opExtrude","CAP_FACE",FACE,{"disambiguationData":[OSD([sQuery(id+"F0.wireOp",EDGE,"E0")])],"isStart":true}),makeQuery(id+"F3.opExtrude","SWEPT_FACE",FACE,{"disambiguationData":[OSD([sQuery(id+"F2.wireOp",EDGE,"E6.1.0.1")])]})]});
            var Q47;
            Q47=makeQuery(id+"F3.boolean.opBoolean","INTERSECT",EDGE,{"derivedFrom":[makeQuery(id+"F1.opExtrude","CAP_FACE",FACE,{"disambiguationData":[OSD([sQuery(id+"F0.wireOp",EDGE,"E0")])],"isStart":true}),makeQuery(id+"F3.opExtrude","SWEPT_FACE",FACE,{"disambiguationData":[OSD([sQuery(id+"F2.wireOp",EDGE,"E6.1.0.2")])]})]});
            var Q48;
            Q48=makeQuery(id+"F3.boolean.opBoolean","INTERSECT",EDGE,{"derivedFrom":[makeQuery(id+"F1.opExtrude","CAP_FACE",FACE,{"disambiguationData":[OSD([sQuery(id+"F0.wireOp",EDGE,"E0")])],"isStart":true}),makeQuery(id+"F3.opExtrude","SWEPT_FACE",FACE,{"disambiguationData":[OSD([sQuery(id+"F2.wireOp",EDGE,"E6.1.0.4")])]})]});
            var Q49;
            Q49=makeQuery(id+"F3.boolean.opBoolean","INTERSECT",EDGE,{"derivedFrom":[makeQuery(id+"F1.opExtrude","CAP_FACE",FACE,{"disambiguationData":[OSD([sQuery(id+"F0.wireOp",EDGE,"E0")])],"isStart":true}),makeQuery(id+"F3.opExtrude","SWEPT_FACE",FACE,{"disambiguationData":[OSD([sQuery(id+"F2.wireOp",EDGE,"E6.1.0.5")])]})]});
            var Q50;
            Q50=makeQuery(id+"F3.boolean.opBoolean","INTERSECT",EDGE,{"derivedFrom":[makeQuery(id+"F1.opExtrude","CAP_FACE",FACE,{"disambiguationData":[OSD([sQuery(id+"F0.wireOp",EDGE,"E0")])],"isStart":true}),makeQuery(id+"F3.opExtrude","SWEPT_FACE",FACE,{"disambiguationData":[OSD([sQuery(id+"F2.wireOp",EDGE,"E6.1.0.7")])]})]});
            var Q51;
            Q51=makeQuery(id+"F3.boolean.opBoolean","INTERSECT",EDGE,{"derivedFrom":[makeQuery(id+"F1.opExtrude","CAP_FACE",FACE,{"disambiguationData":[OSD([sQuery(id+"F0.wireOp",EDGE,"E0")])],"isStart":true}),makeQuery(id+"F3.opExtrude","SWEPT_FACE",FACE,{"disambiguationData":[OSD([sQuery(id+"F2.wireOp",EDGE,"E6.1.0.6")])]})]});
            var Q52;
            Q52=makeQuery(id+"F3.boolean.opBoolean","INTERSECT",EDGE,{"derivedFrom":[makeQuery(id+"F1.opExtrude","CAP_FACE",FACE,{"disambiguationData":[OSD([sQuery(id+"F0.wireOp",EDGE,"E0")])],"isStart":true}),makeQuery(id+"F3.opExtrude","SWEPT_FACE",FACE,{"disambiguationData":[OSD([sQuery(id+"F2.wireOp",EDGE,"E6.1.0.8")])]})]});
            var Q53;
            Q53=makeQuery(id+"F3.boolean.opBoolean","INTERSECT",EDGE,{"derivedFrom":[makeQuery(id+"F1.opExtrude","CAP_FACE",FACE,{"disambiguationData":[OSD([sQuery(id+"F0.wireOp",EDGE,"E0")])],"isStart":true}),makeQuery(id+"F3.opExtrude","SWEPT_FACE",FACE,{"disambiguationData":[OSD([sQuery(id+"F2.wireOp",EDGE,"E6.1.0.10")])]})]});
            var Q54;
            Q54=makeQuery(id+"F3.boolean.opBoolean","INTERSECT",EDGE,{"derivedFrom":[makeQuery(id+"F1.opExtrude","CAP_FACE",FACE,{"disambiguationData":[OSD([sQuery(id+"F0.wireOp",EDGE,"E0")])],"isStart":true}),makeQuery(id+"F3.opExtrude","SWEPT_FACE",FACE,{"disambiguationData":[OSD([sQuery(id+"F2.wireOp",EDGE,"E7")])]})]});
            var Q55;
            Q55=makeQuery(id+"F3.boolean.opBoolean","INTERSECT",EDGE,{"derivedFrom":[makeQuery(id+"F1.opExtrude","CAP_FACE",FACE,{"disambiguationData":[OSD([sQuery(id+"F0.wireOp",EDGE,"E0")])],"isStart":true}),makeQuery(id+"F3.opExtrude","SWEPT_FACE",FACE,{"disambiguationData":[OSD([sQuery(id+"F2.wireOp",EDGE,"E6.1.0.9")])]})]});
            fillet(context, id + "F11", {"entities" : qUnion([Q0, Q1, Q2, Q3, Q4, Q5, Q6, Q7, Q8, Q9, Q10, Q11, Q12, Q13, Q14, Q15, Q16, Q17, Q18, Q19, Q20, Q21, Q22, Q23, Q24, Q25, Q26, Q27, Q28, Q29, Q30, Q31, Q32, Q33, Q34, Q35, Q36, Q37, Q38, Q39, Q40, Q41, Q42, Q43, Q44, Q45, Q46, Q47, Q48, Q49, Q50, Q51, Q52, Q53, Q54, Q55]), "radius" : 0.5 * mm, "tangentPropagation" : true, "allowEdgeOverflow" : false});
        }
    });
